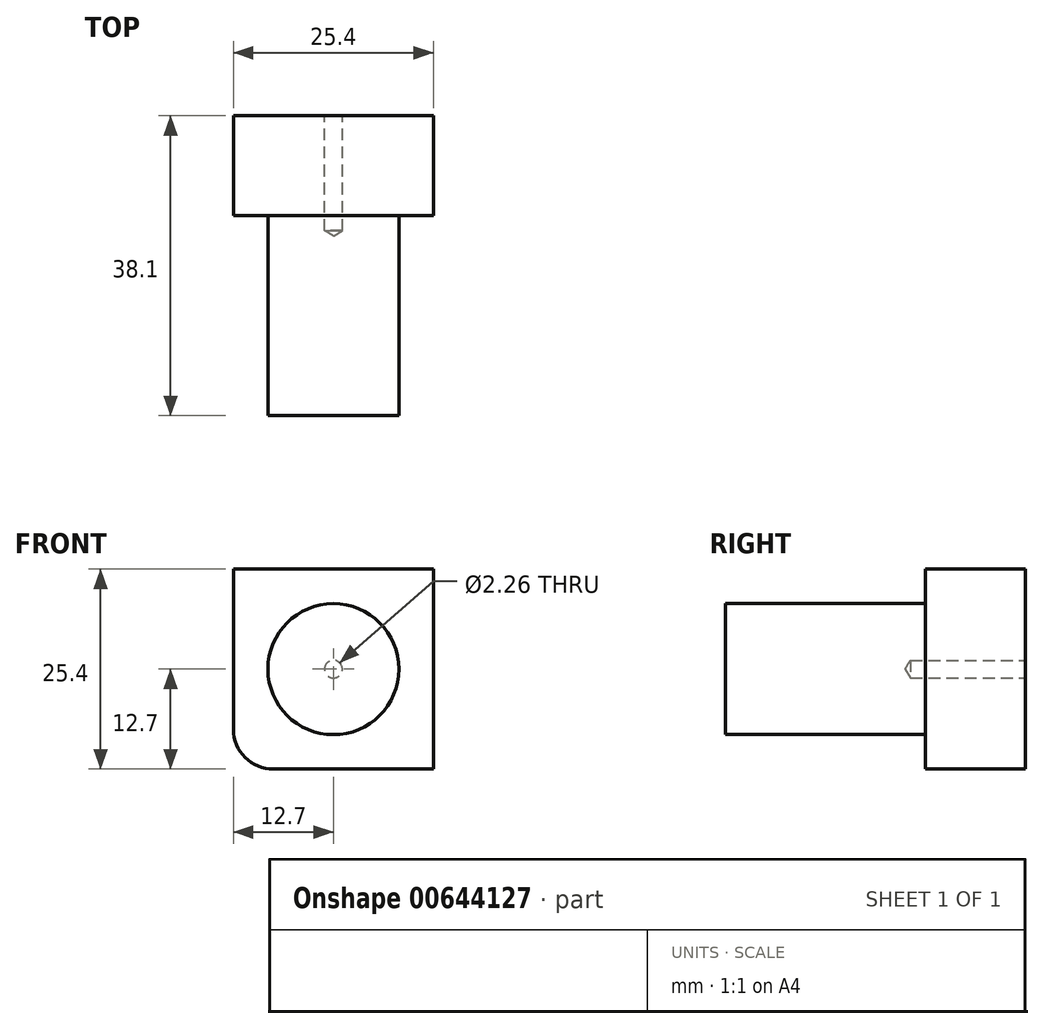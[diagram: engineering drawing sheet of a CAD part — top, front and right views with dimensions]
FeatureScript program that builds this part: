
annotation { "Feature Type Name" : "Feature", "Feature Type Description" : "" }
export const myFeature = defineFeature(function(context is Context, id is Id, definition is map)
    precondition{}
    {
        {
            var Q0;
            Q0=qCreatedBy(makeId("Front.planeOp"),FACE);
            var sketch = newSketch(context, id + "F0", { "sketchPlane" : qUnion([Q0])});
            skLineSegment(sketch, "E0.bottom", {"start": v(12.7, -12.7) * mm, "end": v(-12.7, -12.7) * mm});
            skLineSegment(sketch, "E0.top", {"start": v(12.7, 12.7) * mm, "end": v(-12.7, 12.7) * mm});
            skLineSegment(sketch, "E0.left", {"start": v(12.7, -12.7) * mm, "end": v(12.7, 12.7) * mm});
            skLineSegment(sketch, "E0.right", {"start": v(-12.7, -12.7) * mm, "end": v(-12.7, 12.7) * mm});
            skPoint(sketch, "E0.middle", {"position": v(0, 0) * mm});
            skSolve(sketch);
        }
        {
            var Q0;
            Q0 = qSketchRegion(id + "F0", true);
            extrude(context, id + "F1", {"entities" : qUnion([Q0]), "depth" : 12.7 * mm, "offsetDistance" : 25.4 * mm});
        }
        {
            var Q0;
            Q0=makeQuery(id+"F1.opExtrude","CAP_FACE",FACE,{"disambiguationData":[OSD([sQuery(id+"F0.wireOp",EDGE,"E0.bottom"),sQuery(id+"F0.wireOp",EDGE,"E0.top"),sQuery(id+"F0.wireOp",EDGE,"E0.left"),sQuery(id+"F0.wireOp",EDGE,"E0.right")])],"isStart":false});
            var sketch = newSketch(context, id + "F2", { "sketchPlane" : qUnion([Q0])});
            skCircle(sketch, "E1", {"center": v(0, 0) * mm, "radius": 8.32 * mm});
            skSolve(sketch);
        }
        {
            var Q0;
            Q0 = qSketchRegion(id + "F2", true);
            extrude(context, id + "F3", {"entities" : qUnion([Q0]), "operationType" : NewBodyOperationType.ADD, "depth" : 25.4 * mm, "offsetDistance" : 25.4 * mm});
        }
        {
            var Q0;
            Q0=makeQuery(id+"F1.opExtrude","SWEPT_EDGE",EDGE,{"disambiguationData":[OSD([sQuery(id+"F0.wireOp",EDGE,"E0.bottom"),sQuery(id+"F0.wireOp",EDGE,"E0.right")])]});
            fillet(context, id + "F4", {"entities" : qUnion([Q0]), "radius" : 5.08 * mm, "tangentPropagation" : true, "allowEdgeOverflow" : false});
        }
        {
            var Q0;
            Q0=makeQuery(id+"F1.opExtrude","CAP_FACE",FACE,{"disambiguationData":[OSD([sQuery(id+"F0.wireOp",EDGE,"E0.bottom"),sQuery(id+"F0.wireOp",EDGE,"E0.top"),sQuery(id+"F0.wireOp",EDGE,"E0.left"),sQuery(id+"F0.wireOp",EDGE,"E0.right")])],"isStart":true});
            var sketch = newSketch(context, id + "F5", { "sketchPlane" : qUnion([Q0])});
            skPoint(sketch, "E2", {"position": v(0, 0) * mm});
            skSolve(sketch);
        }
        {
            var Q0;
            Q0=sQuery(id+"F5.wireOp",VERTEX,"E2");
            var Q1;
            Q1=makeQuery(id+"F1.opExtrude","SWEPT_BODY",BODY,{"disambiguationData":[OSD([sQuery(id+"F0.wireOp",EDGE,"E0.bottom"),sQuery(id+"F0.wireOp",EDGE,"E0.top"),sQuery(id+"F0.wireOp",EDGE,"E0.left"),sQuery(id+"F0.wireOp",EDGE,"E0.right")])]});
            hole(context, id + "F6", {"style" : HoleStyle.SIMPLE, "endStyle" : HoleEndStyle.BLIND, "standardTappedOrClearance" : lookupTablePath({ "standard" : "ANSI", "engagement" : "75%", "pitch" : "40 tpi", "size" : "#4", "type" : "Tapped" }), "standardBlindInLast" : lookupTablePath({ "standard" : "ANSI", "engagement" : "75%", "pitch" : "40 tpi", "size" : "#4", "type" : "Tapped" }), "holeDiameter" : 2.26 * mm, "majorDiameter" : 2.84 * mm, "showTappedDepth" : true, "holeDepth" : 14.6 * mm, "tappedDepth" : 12.7 * mm, "tapClearance" : 3, "locations" : qUnion([Q0]), "scope" : qUnion([Q1])});
        }
    });
